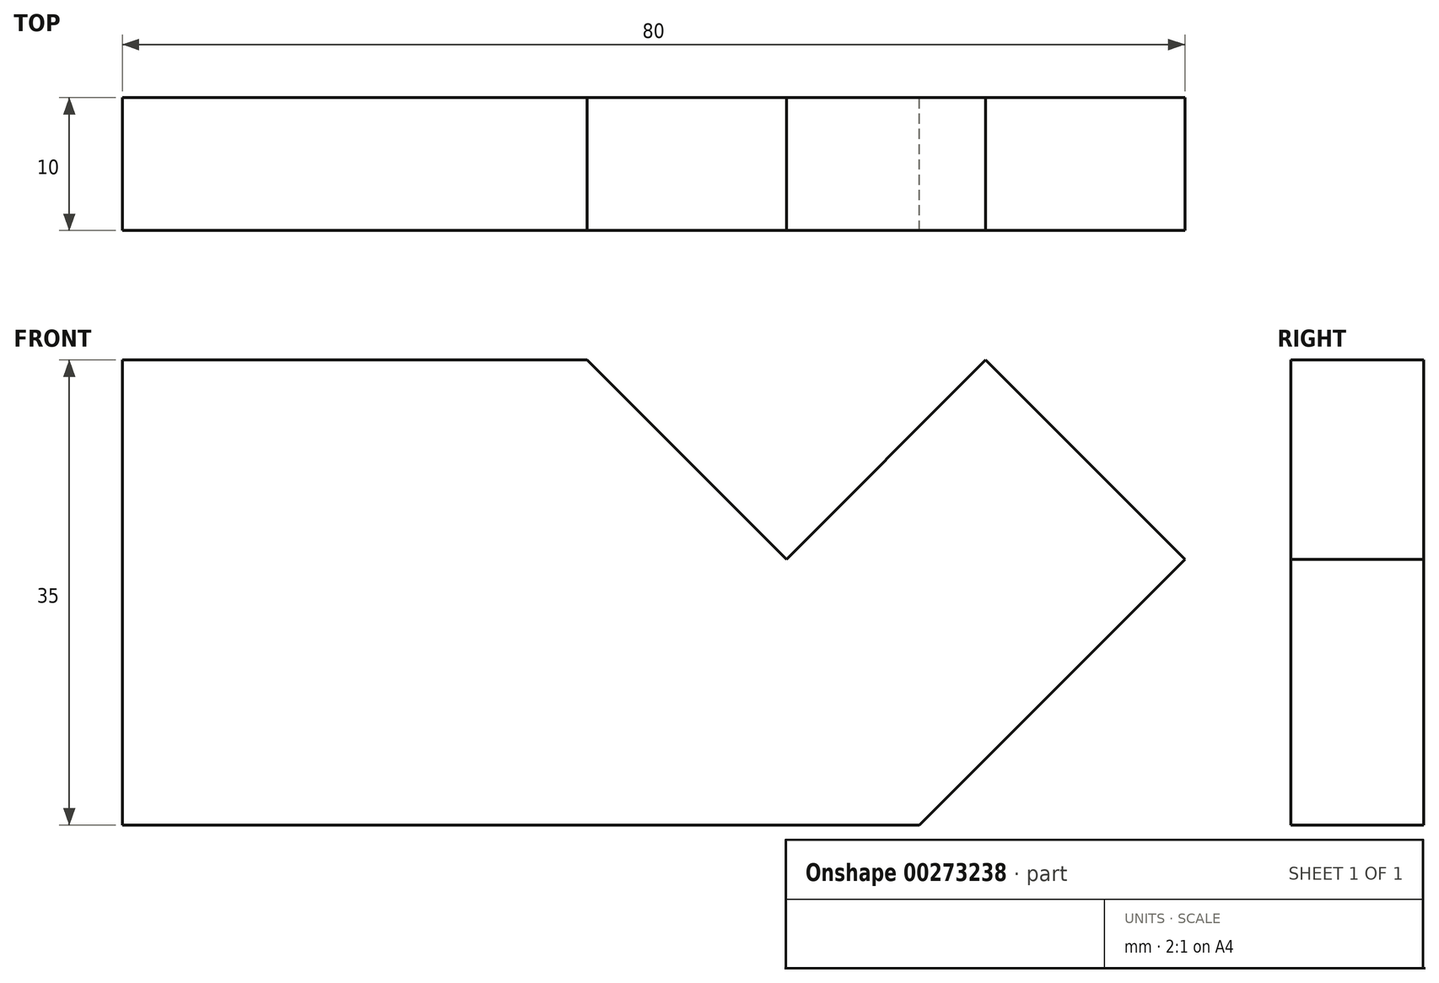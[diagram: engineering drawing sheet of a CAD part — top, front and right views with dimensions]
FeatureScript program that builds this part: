
annotation { "Feature Type Name" : "Feature", "Feature Type Description" : "" }
export const myFeature = defineFeature(function(context is Context, id is Id, definition is map)
    precondition{}
    {
        {
            var Q0;
            Q0=qCreatedBy(makeId("Front.planeOp"),FACE);
            var sketch = newSketch(context, id + "F0", { "sketchPlane" : qUnion([Q0])});
            skLineSegment(sketch, "E0", {"start": v(0, 0) * mm, "end": v(0, 35) * mm});
            skLineSegment(sketch, "E1", {"start": v(0, 35) * mm, "end": v(35, 35) * mm});
            skLineSegment(sketch, "E2", {"start": v(35, 35) * mm, "end": v(50, 20) * mm});
            skLineSegment(sketch, "E3", {"start": v(50, 20) * mm, "end": v(65, 35) * mm});
            skLineSegment(sketch, "E4", {"start": v(65, 35) * mm, "end": v(80, 20) * mm});
            skLineSegment(sketch, "E5", {"start": v(80, 20) * mm, "end": v(60, 0) * mm});
            skLineSegment(sketch, "E6", {"start": v(0, 0) * mm, "end": v(60, 0) * mm});
            skSolve(sketch);
        }
        {
            var Q0;
            Q0 = qSketchRegion(id + "F0", true);
            extrude(context, id + "F1", {"entities" : qUnion([Q0]), "depth" : 10 * mm});
        }
    });
